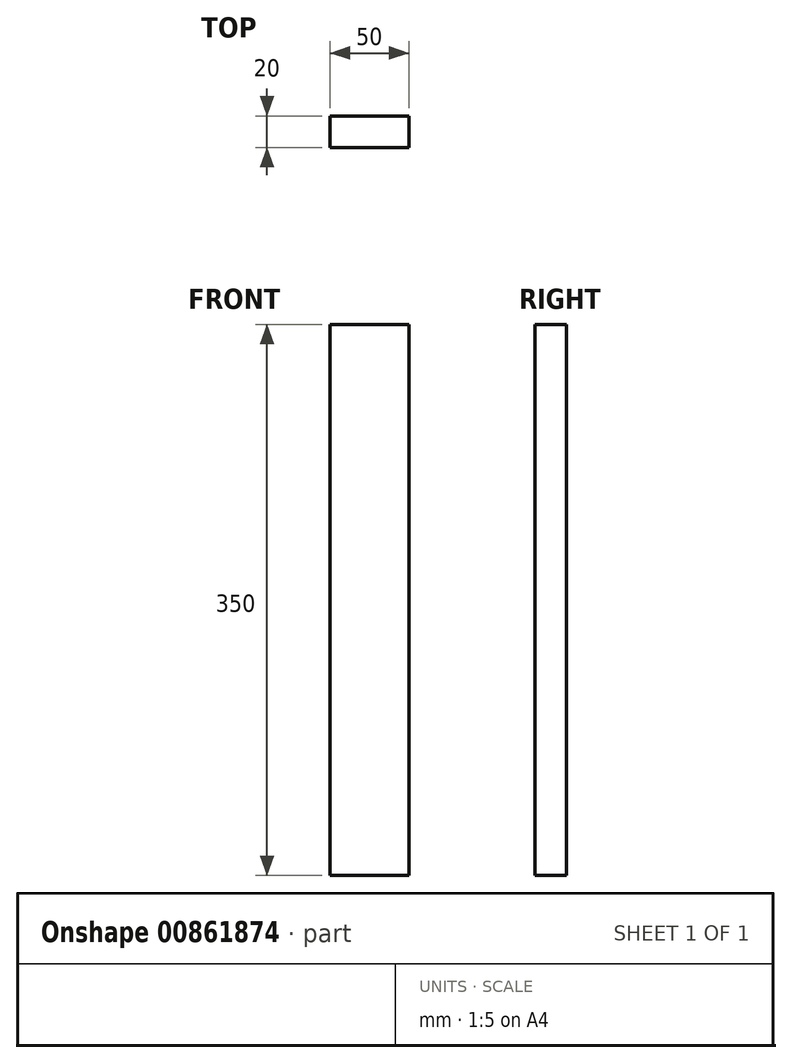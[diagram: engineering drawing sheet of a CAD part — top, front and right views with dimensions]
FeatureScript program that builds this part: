
annotation { "Feature Type Name" : "Feature", "Feature Type Description" : "" }
export const myFeature = defineFeature(function(context is Context, id is Id, definition is map)
    precondition{}
    {
        {
            var Q0;
            Q0=qCreatedBy(makeId("Front.planeOp"),FACE);
            var sketch = newSketch(context, id + "F0", { "sketchPlane" : qUnion([Q0])});
            skLineSegment(sketch, "E0.bottom", {"start": v(25, 175) * mm, "end": v(-25, 175) * mm});
            skLineSegment(sketch, "E0.top", {"start": v(25, -175) * mm, "end": v(-25, -175) * mm});
            skLineSegment(sketch, "E0.left", {"start": v(25, 175) * mm, "end": v(25, -175) * mm});
            skLineSegment(sketch, "E0.right", {"start": v(-25, 175) * mm, "end": v(-25, -175) * mm});
            skPoint(sketch, "E0.middle", {"position": v(0, 0) * mm});
            skSolve(sketch);
        }
        {
            var Q0;
            Q0 = qSketchRegion(id + "F0", true);
            extrude(context, id + "F1", {"entities" : qUnion([Q0]), "depth" : 20 * mm, "offsetDistance" : 25 * mm});
        }
    });
